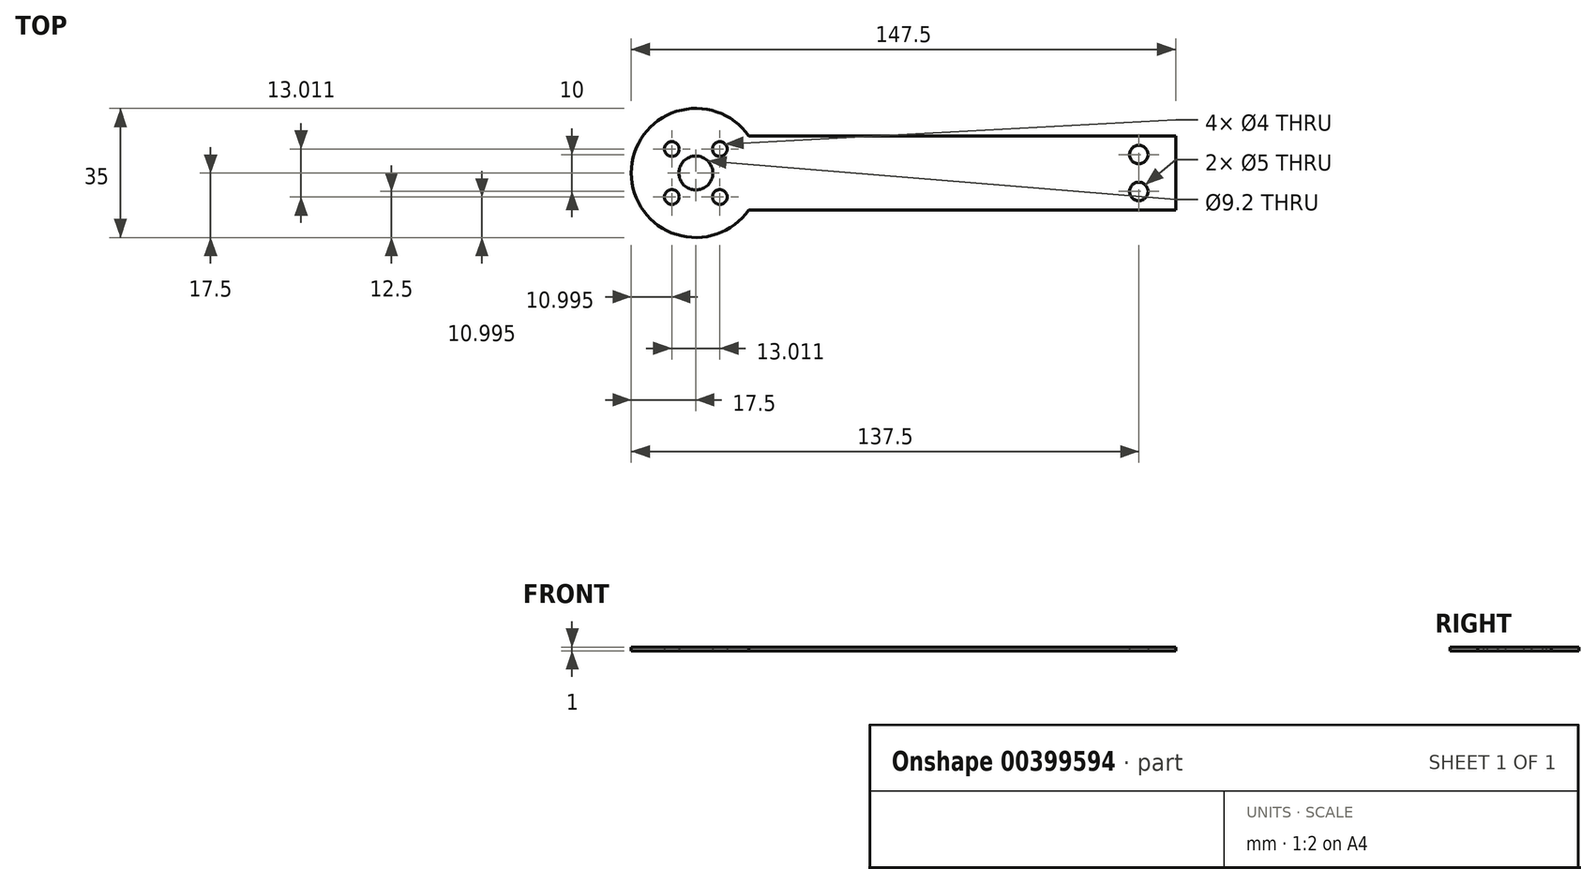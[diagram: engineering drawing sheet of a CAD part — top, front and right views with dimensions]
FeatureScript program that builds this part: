
annotation { "Feature Type Name" : "Feature", "Feature Type Description" : "" }
export const myFeature = defineFeature(function(context is Context, id is Id, definition is map)
    precondition{}
    {
        {
            var Q0;
            Q0=qCreatedBy(makeId("Top.planeOp"),FACE);
            var sketch = newSketch(context, id + "F0", { "sketchPlane" : qUnion([Q0])});
            skLineSegment(sketch, "E0.bottom", {"start": v(60, -10) * mm, "end": v(-55.64, -10) * mm});
            skLineSegment(sketch, "E0.top", {"start": v(60, 10) * mm, "end": v(-55.64, 10) * mm});
            skLineSegment(sketch, "E0.left", {"start": v(60, -10) * mm, "end": v(60, 10) * mm});
            skPoint(sketch, "E0.middle", {"position": v(0, 0) * mm});
            skArc(sketch, "E1", {"start": v(-55.64, 10) * mm, "mid": v(-87.5, 0) * mm, "end": v(-55.64, -10) * mm});
            skCircle(sketch, "E2", {"center": v(-70, 0) * mm, "radius": 4.6 * mm});
            skLineSegment(sketch, "E3", {"start": v(-70, 0) * mm, "end": v(-59.75, 10.25) * mm, "construction": true});
            skCircle(sketch, "E4", {"center": v(-63.5, 6.5) * mm, "radius": 2 * mm});
            skCircle(sketch, "E5.1.0", {"center": v(-63.5, -6.5) * mm, "radius": 2 * mm});
            skCircle(sketch, "E5.2.0", {"center": v(-76.5, -6.5) * mm, "radius": 2 * mm});
            skCircle(sketch, "E5.3.0", {"center": v(-76.5, 6.5) * mm, "radius": 2 * mm});
            skLineSegment(sketch, "E5.anchor1", {"start": v(-70, 0) * mm, "end": v(-63.5, 6.5) * mm, "construction": true});
            skLineSegment(sketch, "E5.anchor2", {"start": v(-70, 0) * mm, "end": v(-76.5, 6.5) * mm, "construction": true});
            skCircle(sketch, "E6", {"center": v(50, 5) * mm, "radius": 2.5 * mm});
            skCircle(sketch, "E7.MirrorC", {"center": v(50, -5) * mm, "radius": 2.5 * mm});
            skSolve(sketch);
        }
        {
            var Q0;
            Q0 = qSketchRegion(id + "F0", true);
            extrude(context, id + "F1", {"entities" : qUnion([Q0]), "depth" : 1 * mm});
        }
    });
